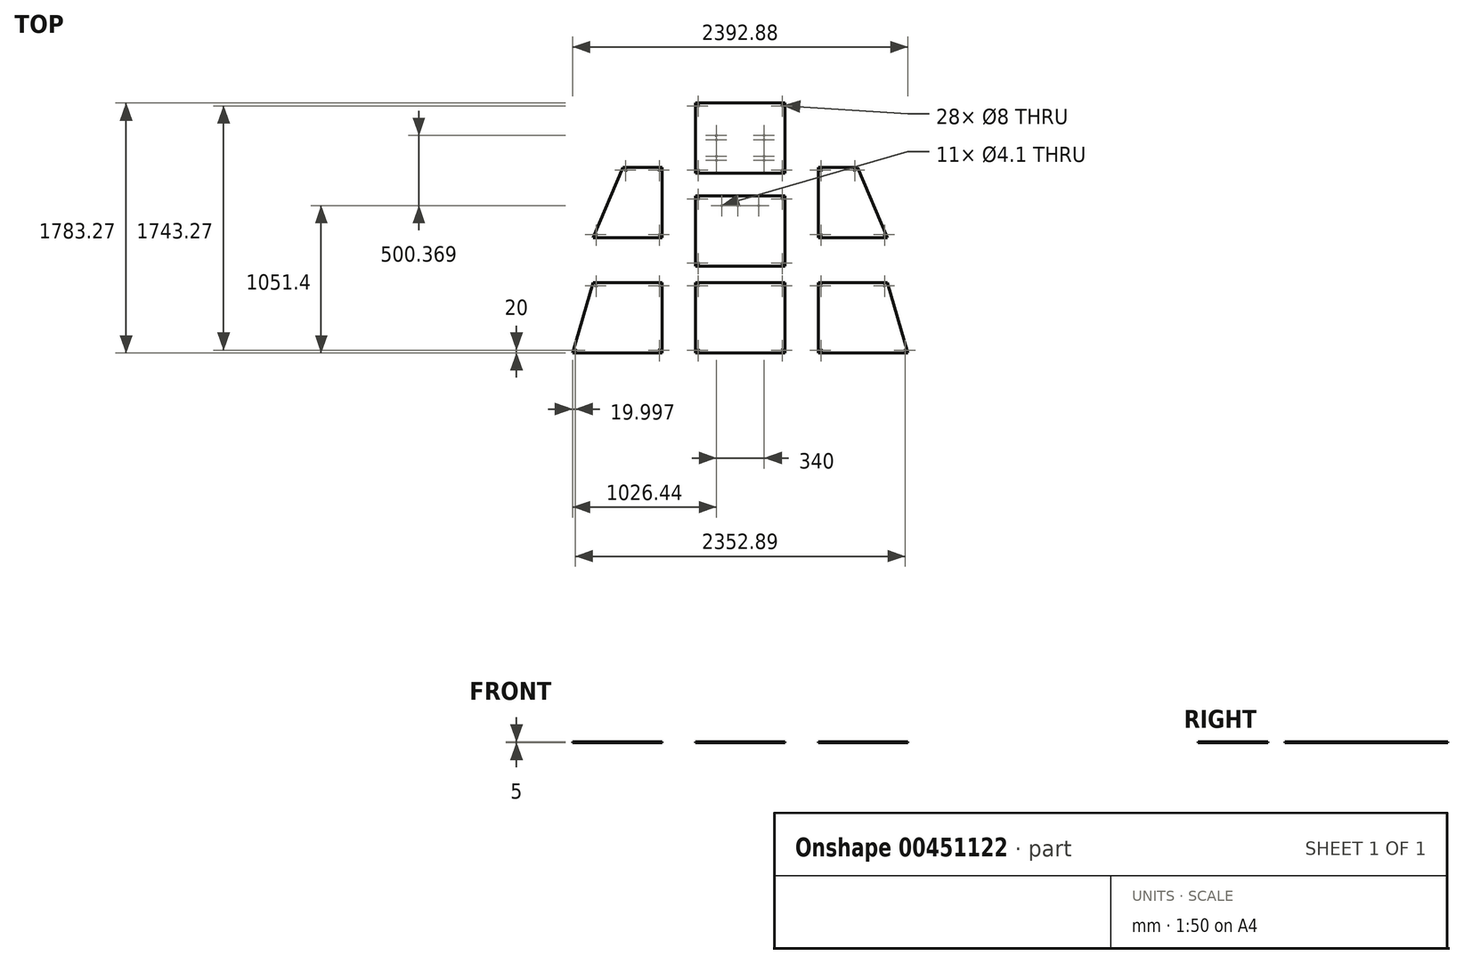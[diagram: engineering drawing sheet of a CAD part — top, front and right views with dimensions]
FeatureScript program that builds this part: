
annotation { "Feature Type Name" : "Feature", "Feature Type Description" : "" }
export const myFeature = defineFeature(function(context is Context, id is Id, definition is map)
    precondition{}
    {
        {
            var Q0;
            Q0=qCreatedBy(makeId("Top.planeOp"),FACE);
            var sketch = newSketch(context, id + "F0", { "sketchPlane" : qUnion([Q0])});
            skLineSegment(sketch, "E0.bottom", {"start": v(320, -250) * mm, "end": v(-320, -250) * mm});
            skLineSegment(sketch, "E0.top", {"start": v(320, 250) * mm, "end": v(-320, 250) * mm});
            skLineSegment(sketch, "E0.left", {"start": v(320, -250) * mm, "end": v(320, 250) * mm});
            skLineSegment(sketch, "E0.right", {"start": v(-320, -250) * mm, "end": v(-320, 250) * mm});
            skPoint(sketch, "E0.middle", {"position": v(0, 0) * mm});
            skCircle(sketch, "E1", {"center": v(300, 230) * mm, "radius": 4 * mm});
            skCircle(sketch, "E2", {"center": v(-300, 230) * mm, "radius": 4 * mm});
            skCircle(sketch, "E3", {"center": v(300, -230) * mm, "radius": 4 * mm});
            skCircle(sketch, "E4", {"center": v(-300, -230) * mm, "radius": 4 * mm});
            skSolve(sketch);
        }
        {
            var Q0;
            Q0 = qSketchRegion(id + "F0", true);
            extrude(context, id + "F1", {"entities" : qUnion([Q0]), "depth" : 5 * mm});
        }
        {
            var Q0;
            Q0=qCreatedBy(makeId("Top.planeOp"),FACE);
            var sketch = newSketch(context, id + "F2", { "sketchPlane" : qUnion([Q0])});
            skLineSegment(sketch, "E5.top", {"start": v(-556.44, 250) * mm, "end": v(-1048.94, 250) * mm});
            skLineSegment(sketch, "E5.left", {"start": v(-556.44, -250) * mm, "end": v(-556.44, 250) * mm});
            skPoint(sketch, "E5.middle", {"position": v(-802.7, 0) * mm});
            skLineSegment(sketch, "E6", {"start": v(-556.44, -250) * mm, "end": v(-1196.44, -250) * mm});
            skLineSegment(sketch, "E7", {"start": v(-1196.44, -250) * mm, "end": v(-1048.94, 250) * mm});
            skCircle(sketch, "E8", {"center": v(-576.44, 230) * mm, "radius": 4 * mm});
            skCircle(sketch, "E9", {"center": v(-576.44, -230) * mm, "radius": 4 * mm});
            skCircle(sketch, "E10", {"center": v(-1176.44, -230) * mm, "radius": 4 * mm});
            skCircle(sketch, "E11", {"center": v(-1028.94, 230) * mm, "radius": 4 * mm});
            skLineSegment(sketch, "E12.bottom", {"start": v(-556.44, 573.43) * mm, "end": v(-1048.94, 573.43) * mm});
            skLineSegment(sketch, "E12.left", {"start": v(-556.44, 573.43) * mm, "end": v(-556.44, 1073.43) * mm});
            skPoint(sketch, "E12.middle", {"position": v(-802.7, 823.43) * mm});
            skLineSegment(sketch, "E13", {"start": v(-556.44, 1073.43) * mm, "end": v(-836.44, 1073.43) * mm});
            skLineSegment(sketch, "E14", {"start": v(-1048.94, 573.43) * mm, "end": v(-836.44, 1073.43) * mm});
            skCircle(sketch, "E15", {"center": v(-576.44, 1053.43) * mm, "radius": 4 * mm});
            skCircle(sketch, "E16", {"center": v(-576.44, 593.43) * mm, "radius": 4 * mm});
            skCircle(sketch, "E17", {"center": v(-1028.94, 593.43) * mm, "radius": 4 * mm});
            skCircle(sketch, "E18", {"center": v(-816.44, 1053.43) * mm, "radius": 4 * mm});
            skSolve(sketch);
        }
        {
            var Q0;
            Q0 = qSketchRegion(id + "F2", true);
            extrude(context, id + "F3", {"entities" : qUnion([Q0]), "depth" : 5 * mm});
        }
        {
            var Q0;
            Q0=makeQuery(id+"F3.opExtrude","SWEPT_BODY",BODY,{"disambiguationData":[OSD([sQuery(id+"F2.wireOp",EDGE,"E5.top"),sQuery(id+"F2.wireOp",EDGE,"E5.left"),sQuery(id+"F2.wireOp",EDGE,"E6"),sQuery(id+"F2.wireOp",EDGE,"E7"),sQuery(id+"F2.wireOp",EDGE,"E8"),sQuery(id+"F2.wireOp",EDGE,"E9"),sQuery(id+"F2.wireOp",EDGE,"E10"),sQuery(id+"F2.wireOp",EDGE,"E11")])]});
            var Q1;
            Q1=makeQuery(id+"F3.opExtrude","SWEPT_BODY",BODY,{"disambiguationData":[OSD([sQuery(id+"F2.wireOp",EDGE,"E12.bottom"),sQuery(id+"F2.wireOp",EDGE,"E12.left"),sQuery(id+"F2.wireOp",EDGE,"E13"),sQuery(id+"F2.wireOp",EDGE,"E14"),sQuery(id+"F2.wireOp",EDGE,"E15"),sQuery(id+"F2.wireOp",EDGE,"E16"),sQuery(id+"F2.wireOp",EDGE,"E17"),sQuery(id+"F2.wireOp",EDGE,"E18")])]});
            var Q2;
            Q2=qCreatedBy(makeId("Right.planeOp"),FACE);
            mirror(context, id + "F4", {"entities" : qUnion([Q0, Q1]), "mirrorPlane" : qUnion([Q2])});
        }
        {
            var Q0;
            Q0=qCreatedBy(makeId("Top.planeOp"),FACE);
            var sketch = newSketch(context, id + "F5", { "sketchPlane" : qUnion([Q0])});
            skLineSegment(sketch, "E19.bottom", {"start": v(320, 869.9) * mm, "end": v(-320, 869.9) * mm});
            skLineSegment(sketch, "E19.top", {"start": v(320, 369.9) * mm, "end": v(-320, 369.9) * mm});
            skLineSegment(sketch, "E19.left", {"start": v(320, 869.9) * mm, "end": v(320, 369.9) * mm});
            skLineSegment(sketch, "E19.right", {"start": v(-320, 869.9) * mm, "end": v(-320, 369.9) * mm});
            skPoint(sketch, "E19.middle", {"position": v(0, 619.9) * mm});
            skCircle(sketch, "E20", {"center": v(-132.5, 801.4) * mm, "radius": 2.05 * mm});
            skCircle(sketch, "E21", {"center": v(-17.5, 801.4) * mm, "radius": 2.05 * mm});
            skCircle(sketch, "E22", {"center": v(132.5, 801.4) * mm, "radius": 2.05 * mm});
            skCircle(sketch, "E23", {"center": v(-300, 849.9) * mm, "radius": 4 * mm});
            skCircle(sketch, "E24", {"center": v(300, 849.9) * mm, "radius": 4 * mm});
            skCircle(sketch, "E25", {"center": v(-300, 389.9) * mm, "radius": 4 * mm});
            skCircle(sketch, "E26", {"center": v(300, 389.9) * mm, "radius": 4 * mm});
            skSolve(sketch);
        }
        {
            var Q0;
            Q0 = qSketchRegion(id + "F5", true);
            extrude(context, id + "F6", {"entities" : qUnion([Q0]), "depth" : 5 * mm});
        }
        {
            var Q0;
            Q0=qCreatedBy(makeId("Top.planeOp"),FACE);
            var sketch = newSketch(context, id + "F7", { "sketchPlane" : qUnion([Q0])});
            skLineSegment(sketch, "E27.bottom", {"start": v(320, 1033.27) * mm, "end": v(-320, 1033.27) * mm});
            skLineSegment(sketch, "E27.top", {"start": v(320, 1533.27) * mm, "end": v(-320, 1533.27) * mm});
            skLineSegment(sketch, "E27.left", {"start": v(320, 1033.27) * mm, "end": v(320, 1533.27) * mm});
            skLineSegment(sketch, "E27.right", {"start": v(-320, 1033.27) * mm, "end": v(-320, 1533.27) * mm});
            skPoint(sketch, "E27.middle", {"position": v(0, 1283.27) * mm});
            skCircle(sketch, "E28", {"center": v(170, 1153.77) * mm, "radius": 2.05 * mm});
            skCircle(sketch, "E29", {"center": v(170, 1123.77) * mm, "radius": 2.05 * mm});
            skCircle(sketch, "E30", {"center": v(170, 1271.77) * mm, "radius": 2.05 * mm});
            skCircle(sketch, "E31", {"center": v(170, 1301.77) * mm, "radius": 2.05 * mm});
            skCircle(sketch, "E32.MirrorC", {"center": v(-170, 1153.77) * mm, "radius": 2.05 * mm});
            skCircle(sketch, "E33.MirrorC", {"center": v(-170, 1271.77) * mm, "radius": 2.05 * mm});
            skCircle(sketch, "E34.MirrorC", {"center": v(-170, 1301.77) * mm, "radius": 2.05 * mm});
            skCircle(sketch, "E35.MirrorC", {"center": v(-170, 1123.77) * mm, "radius": 2.05 * mm});
            skCircle(sketch, "E36", {"center": v(-300, 1513.27) * mm, "radius": 4 * mm});
            skCircle(sketch, "E37", {"center": v(300, 1513.27) * mm, "radius": 4 * mm});
            skCircle(sketch, "E38", {"center": v(-300, 1053.27) * mm, "radius": 4 * mm});
            skCircle(sketch, "E39", {"center": v(300, 1053.27) * mm, "radius": 4 * mm});
            skSolve(sketch);
        }
        {
            var Q0;
            Q0 = qSketchRegion(id + "F7", true);
            extrude(context, id + "F8", {"entities" : qUnion([Q0]), "depth" : 5 * mm});
        }
    });
